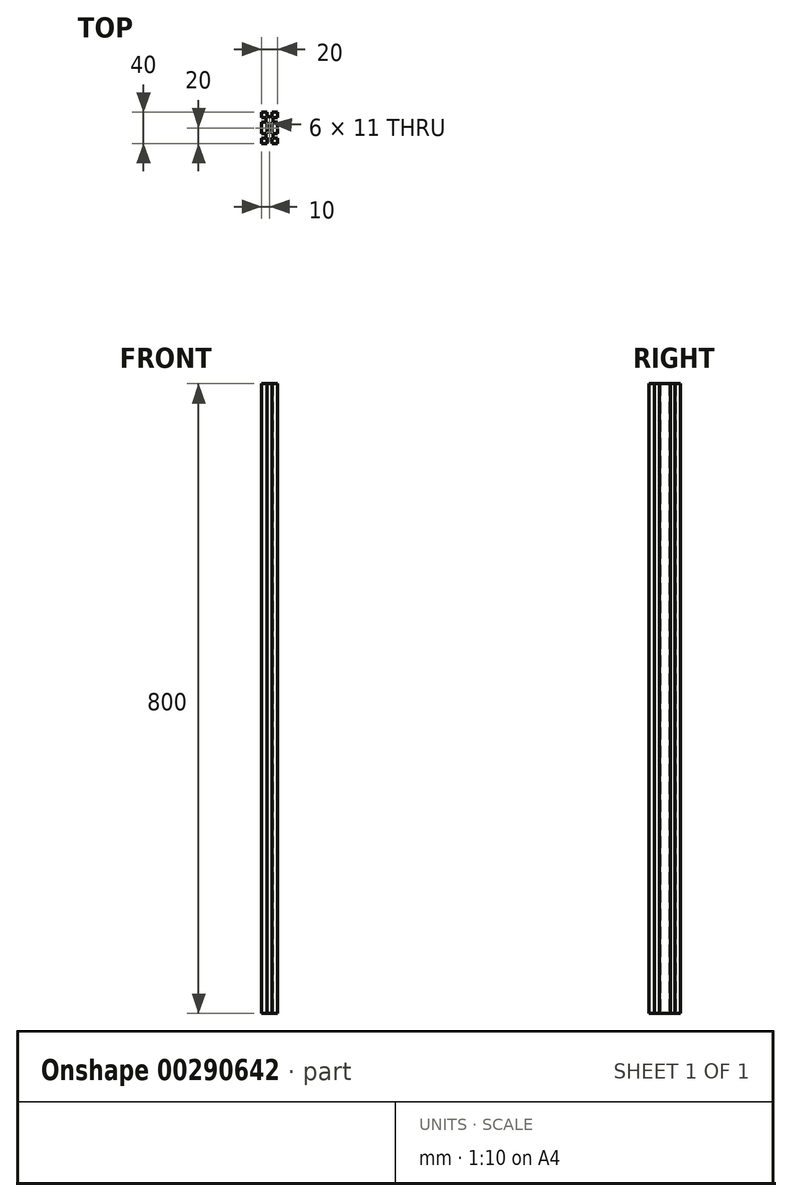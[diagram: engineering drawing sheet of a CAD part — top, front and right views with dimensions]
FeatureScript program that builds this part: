
annotation { "Feature Type Name" : "Feature", "Feature Type Description" : "" }
export const myFeature = defineFeature(function(context is Context, id is Id, definition is map)
    precondition{}
    {
        {
            var Q0;
            Q0=qCreatedBy(makeId("Top.planeOp"),FACE);
            var sketch = newSketch(context, id + "F0", { "sketchPlane" : qUnion([Q0])});
            skLineSegment(sketch, "E0.bottom", {"start": v(0, 0) * mm, "end": v(7, 0) * mm});
            skLineSegment(sketch, "E0.top", {"start": v(0, 20) * mm, "end": v(20, 20) * mm});
            skLineSegment(sketch, "E0.left", {"start": v(0, 0) * mm, "end": v(0, 20) * mm});
            skLineSegment(sketch, "E0.right", {"start": v(20, 0) * mm, "end": v(20, 20) * mm});
            skLineSegment(sketch, "E1.bottom", {"start": v(7, 20) * mm, "end": v(13, 20) * mm});
            skLineSegment(sketch, "E1.top", {"start": v(7, 14.5) * mm, "end": v(13, 14.5) * mm});
            skLineSegment(sketch, "E1.left", {"start": v(7, 20) * mm, "end": v(7, 14.5) * mm});
            skLineSegment(sketch, "E1.right", {"start": v(13, 20) * mm, "end": v(13, 14.5) * mm});
            skLineSegment(sketch, "E2.bottom", {"start": v(20, 13) * mm, "end": v(14.5, 13) * mm});
            skLineSegment(sketch, "E2.top", {"start": v(20, 7) * mm, "end": v(14.5, 7) * mm});
            skLineSegment(sketch, "E2.left", {"start": v(20, 13) * mm, "end": v(20, 7) * mm});
            skLineSegment(sketch, "E2.right", {"start": v(14.5, 13) * mm, "end": v(14.5, 7) * mm});
            skLineSegment(sketch, "E3.top", {"start": v(13, 5.5) * mm, "end": v(7, 5.5) * mm});
            skLineSegment(sketch, "E3.left", {"start": v(13, 0) * mm, "end": v(13, 5.5) * mm});
            skLineSegment(sketch, "E3.right", {"start": v(7, 0) * mm, "end": v(7, 5.5) * mm});
            skLineSegment(sketch, "E4.bottom", {"start": v(0, 7) * mm, "end": v(5.5, 7) * mm});
            skLineSegment(sketch, "E4.top", {"start": v(0, 13) * mm, "end": v(5.5, 13) * mm});
            skLineSegment(sketch, "E4.left", {"start": v(0, 7) * mm, "end": v(0, 13) * mm});
            skLineSegment(sketch, "E4.right", {"start": v(5.5, 7) * mm, "end": v(5.5, 13) * mm});
            skLineSegment(sketch, "E5.MirrorCS", {"start": v(5.5, -7) * mm, "end": v(5.5, -13) * mm});
            skLineSegment(sketch, "E6.MirrorCS", {"start": v(13, -5.5) * mm, "end": v(7, -5.5) * mm});
            skLineSegment(sketch, "E7.MirrorCS", {"start": v(13, 0) * mm, "end": v(13, -5.5) * mm});
            skLineSegment(sketch, "E8.MirrorCS", {"start": v(7, 0) * mm, "end": v(7, -5.5) * mm});
            skLineSegment(sketch, "E9.MirrorCS", {"start": v(0, -20) * mm, "end": v(20, -20) * mm});
            skLineSegment(sketch, "E10.MirrorCS", {"start": v(0, 0) * mm, "end": v(0, -20) * mm});
            skLineSegment(sketch, "E11.MirrorCS", {"start": v(20, 0) * mm, "end": v(20, -20) * mm});
            skLineSegment(sketch, "E12.MirrorCS", {"start": v(7, -20) * mm, "end": v(13, -20) * mm});
            skLineSegment(sketch, "E13.MirrorCS", {"start": v(7, -14.5) * mm, "end": v(13, -14.5) * mm});
            skLineSegment(sketch, "E14.MirrorCS", {"start": v(7, -20) * mm, "end": v(7, -14.5) * mm});
            skLineSegment(sketch, "E15.MirrorCS", {"start": v(13, -20) * mm, "end": v(13, -14.5) * mm});
            skLineSegment(sketch, "E16.MirrorCS", {"start": v(20, -13) * mm, "end": v(14.5, -13) * mm});
            skLineSegment(sketch, "E17.MirrorCS", {"start": v(20, -7) * mm, "end": v(14.5, -7) * mm});
            skLineSegment(sketch, "E18.MirrorCS", {"start": v(20, -13) * mm, "end": v(20, -7) * mm});
            skLineSegment(sketch, "E19.MirrorCS", {"start": v(14.5, -13) * mm, "end": v(14.5, -7) * mm});
            skLineSegment(sketch, "E20.MirrorCS", {"start": v(0, -7) * mm, "end": v(5.5, -7) * mm});
            skLineSegment(sketch, "E21.MirrorCS", {"start": v(0, -13) * mm, "end": v(5.5, -13) * mm});
            skLineSegment(sketch, "E22.MirrorCS", {"start": v(0, -7) * mm, "end": v(0, -13) * mm});
            skLineSegment(sketch, "E23.trimOffspring", {"start": v(13, 0) * mm, "end": v(20, 0) * mm});
            skSolve(sketch);
        }
        {
            var Q0;
            Q0=makeQuery(id+"F0.imprint","IMPRINT",FACE,{"disambiguationData":[TD([[makeQuery(id+"F0.imprint","IMPRINT",EDGE,{"derivedFrom":sQuery(id+"F0.wireOp",EDGE,"E1.top")}),-1.0]])]});
            var Q1;
            Q1=makeQuery(id+"F0.imprint","IMPRINT",FACE,{"disambiguationData":[TD([[makeQuery(id+"F0.imprint","IMPRINT",EDGE,{"derivedFrom":sQuery(id+"F0.wireOp",EDGE,"E5.MirrorCS")}),1.0]])]});
            extrude(context, id + "F1", {"entities" : qUnion([Q0, Q1]), "depth" : 800 * mm});
        }
    });
